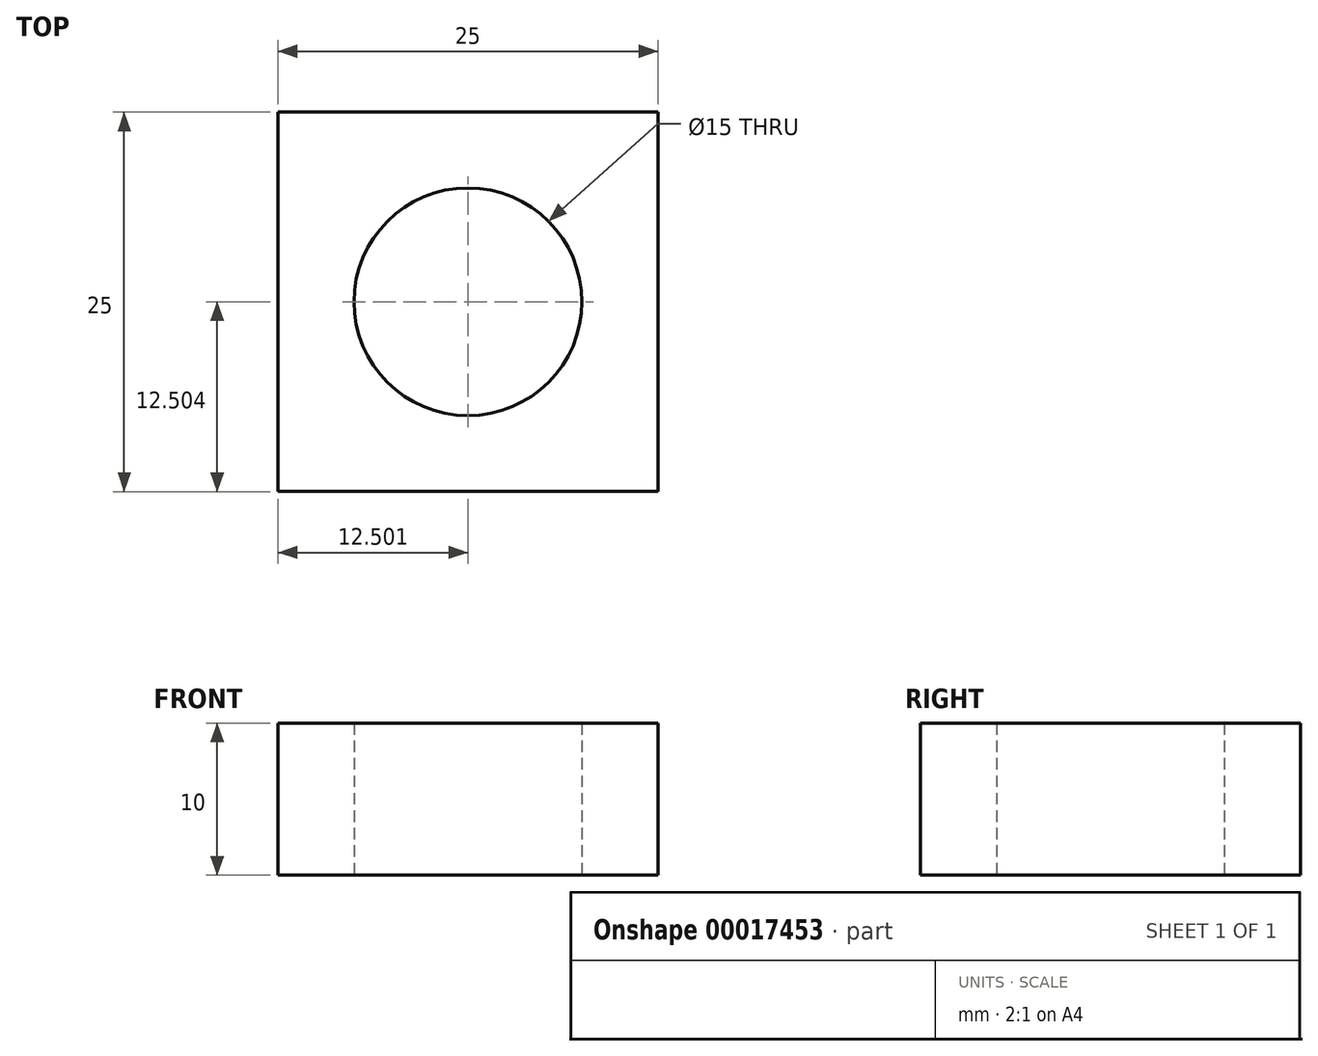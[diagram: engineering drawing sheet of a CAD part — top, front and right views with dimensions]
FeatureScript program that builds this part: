
annotation { "Feature Type Name" : "Feature", "Feature Type Description" : "" }
export const myFeature = defineFeature(function(context is Context, id is Id, definition is map)
    precondition{}
    {
        {
            var Q0;
            Q0=qCreatedBy(makeId("Top.planeOp"),FACE);
            var sketch = newSketch(context, id + "F0", { "sketchPlane" : qUnion([Q0])});
            skLineSegment(sketch, "E0", {"start": v(-16.69, 6.38) * mm, "end": v(8.31, 6.38) * mm});
            skLineSegment(sketch, "E1", {"start": v(-16.69, 6.38) * mm, "end": v(-16.69, -18.62) * mm});
            skLineSegment(sketch, "E2", {"start": v(8.31, 6.38) * mm, "end": v(8.31, -18.62) * mm});
            skLineSegment(sketch, "E3", {"start": v(-16.69, -18.62) * mm, "end": v(8.31, -18.62) * mm});
            skCircle(sketch, "E4", {"center": v(-4.19, -6.12) * mm, "radius": 7.5 * mm});
            skSolve(sketch);
        }
        {
            var Q0;
            Q0 = qSketchRegion(id + "F0", true);
            extrude(context, id + "F1", {"entities" : qUnion([Q0]), "depth" : 10 * mm});
        }
    });
